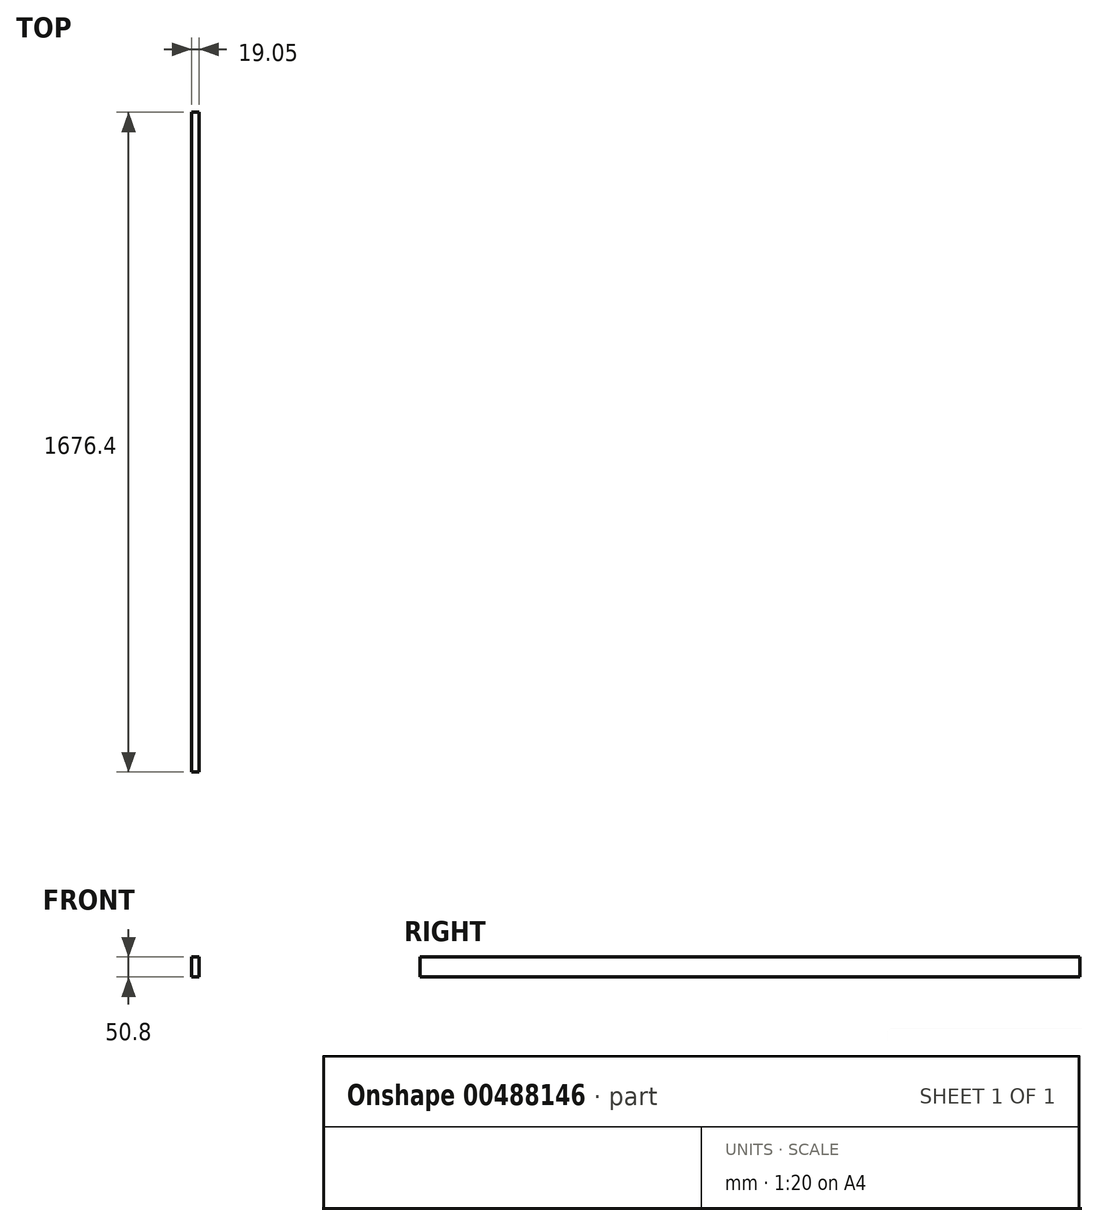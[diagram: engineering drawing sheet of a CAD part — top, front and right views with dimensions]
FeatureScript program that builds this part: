
annotation { "Feature Type Name" : "Feature", "Feature Type Description" : "" }
export const myFeature = defineFeature(function(context is Context, id is Id, definition is map)
    precondition{}
    {
        {
            var Q0;
            Q0=qCreatedBy(makeId("Front.planeOp"),FACE);
            var sketch = newSketch(context, id + "F0", { "sketchPlane" : qUnion([Q0])});
            skLineSegment(sketch, "E0", {"start": v(0, 0) * mm, "end": v(19.05, 0) * mm});
            skLineSegment(sketch, "E1", {"start": v(0, 0) * mm, "end": v(0, -50.8) * mm});
            skLineSegment(sketch, "E2", {"start": v(0, -50.8) * mm, "end": v(19.05, -50.8) * mm});
            skLineSegment(sketch, "E3", {"start": v(19.05, -50.8) * mm, "end": v(19.05, 0) * mm});
            skSolve(sketch);
        }
        {
            var Q0;
            Q0=makeQuery(id+"F0.imprint","IMPRINT",FACE,{"disambiguationData":[TD([[makeQuery(id+"F0.imprint","IMPRINT",EDGE,{"derivedFrom":sQuery(id+"F0.wireOp",EDGE,"E0")}),-1.0]])]});
            extrude(context, id + "F1", {"entities" : qUnion([Q0]), "oppositeDirection" : true, "depth" : (1524 * mm + 152.4 * mm), "offsetDistance" : 25.4 * mm});
        }
    });
